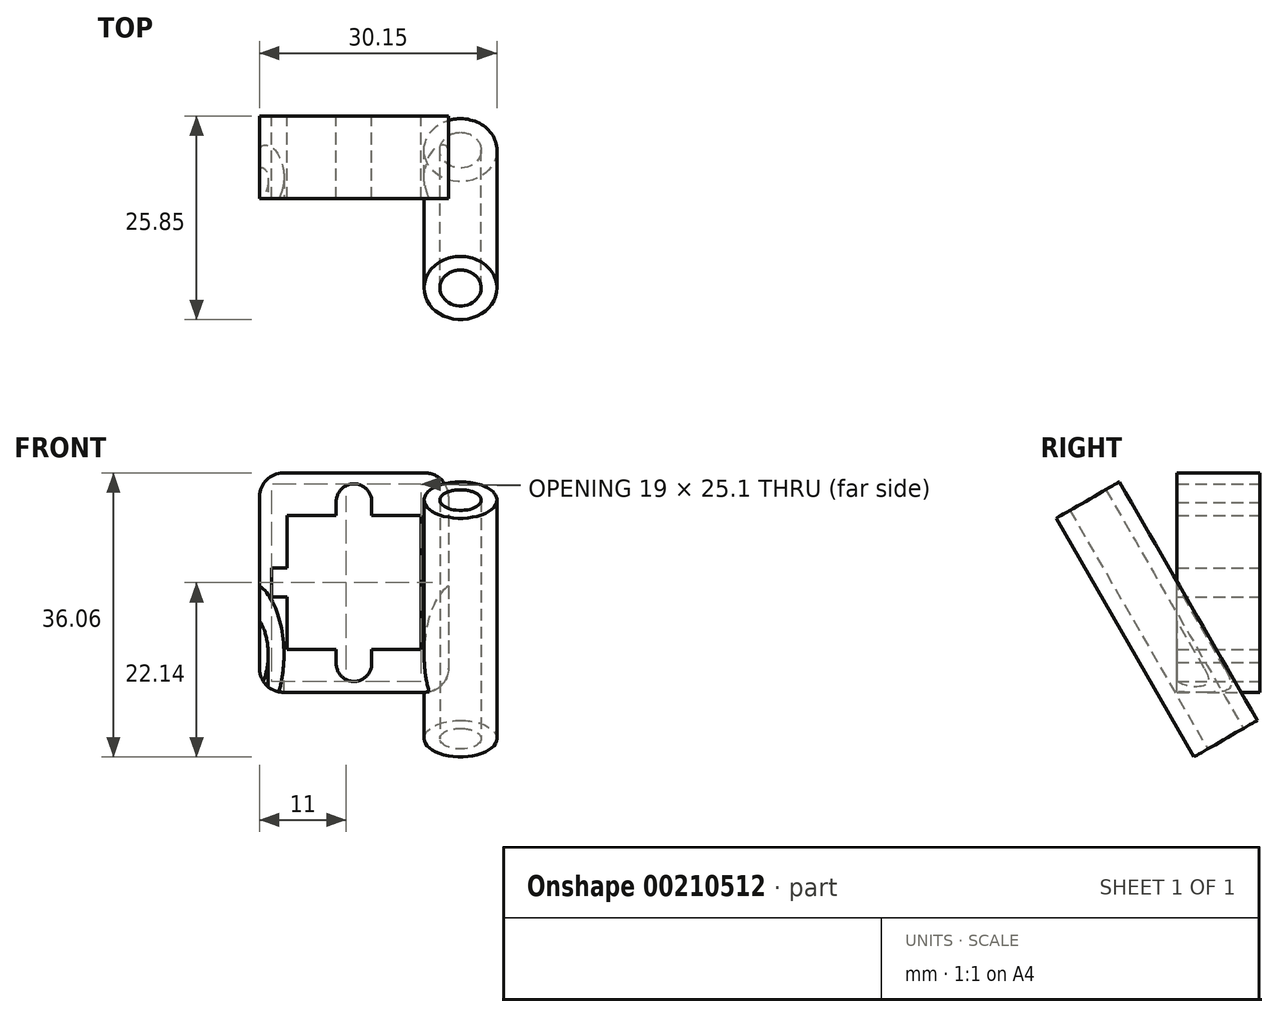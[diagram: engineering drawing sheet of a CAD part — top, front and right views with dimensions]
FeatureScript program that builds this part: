
annotation { "Feature Type Name" : "Feature", "Feature Type Description" : "" }
export const myFeature = defineFeature(function(context is Context, id is Id, definition is map)
    precondition{}
    {
        {
            var Q0;
            Q0=qCreatedBy(makeId("Front.planeOp"),FACE);
            var sketch = newSketch(context, id + "F0", { "sketchPlane" : qUnion([Q0])});
            skLineSegment(sketch, "E0.bottom", {"start": v(8.5, -8.5) * mm, "end": v(2.25, -8.5) * mm});
            skLineSegment(sketch, "E0.top", {"start": v(8.5, 8.5) * mm, "end": v(2.25, 8.5) * mm});
            skLineSegment(sketch, "E0.left", {"start": v(8.5, -8.5) * mm, "end": v(8.5, 8.5) * mm});
            skLineSegment(sketch, "E0.right", {"start": v(-8.5, -8.5) * mm, "end": v(-8.5, -1.85) * mm});
            skPoint(sketch, "E0.middle", {"position": v(0, 0) * mm});
            skLineSegment(sketch, "E1.left", {"start": v(2.25, 10.16) * mm, "end": v(2.25, 8.5) * mm});
            skLineSegment(sketch, "E1.right", {"start": v(-2.25, 10.16) * mm, "end": v(-2.25, 8.5) * mm});
            skLineSegment(sketch, "E2.bottom", {"start": v(-10.5, -1.85) * mm, "end": v(-8.5, -1.85) * mm});
            skLineSegment(sketch, "E2.top", {"start": v(-10.5, 1.85) * mm, "end": v(-8.5, 1.85) * mm});
            skLineSegment(sketch, "E2.left", {"start": v(-10.5, -1.85) * mm, "end": v(-10.5, 1.85) * mm});
            skLineSegment(sketch, "E3.trimOffspring", {"start": v(-2.25, -8.5) * mm, "end": v(-2.25, -10.16) * mm});
            skLineSegment(sketch, "E4.trimOffspring", {"start": v(2.25, -8.5) * mm, "end": v(2.25, -10.16) * mm});
            skLineSegment(sketch, "E5.trimOffspring", {"start": v(-2.25, 8.5) * mm, "end": v(-8.5, 8.5) * mm});
            skLineSegment(sketch, "E6.trimOffspring", {"start": v(-2.25, -8.5) * mm, "end": v(-8.5, -8.5) * mm});
            skLineSegment(sketch, "E7.trimOffspring", {"start": v(-8.5, 1.85) * mm, "end": v(-8.5, 8.5) * mm});
            skArc(sketch, "E8", {"start": v(2.25, 10.16) * mm, "mid": v(0, 12.55) * mm, "end": v(-2.25, 10.16) * mm});
            skPoint(sketch, "E8.first.point", {"position": v(0, 12.55) * mm});
            skPoint(sketch, "E8.second.point", {"position": v(-2.25, 10.16) * mm});
            skPoint(sketch, "E8.third.point", {"position": v(2.25, 10.16) * mm});
            skArc(sketch, "E9.MirrorCS", {"start": v(2.25, -10.16) * mm, "mid": v(0, -12.55) * mm, "end": v(-2.25, -10.16) * mm});
            skLineSegment(sketch, "E10.bottom", {"start": v(9, 13.92) * mm, "end": v(-9, 13.92) * mm});
            skLineSegment(sketch, "E10.top", {"start": v(9, -13.92) * mm, "end": v(-9, -13.92) * mm});
            skLineSegment(sketch, "E10.left", {"start": v(12, 10.92) * mm, "end": v(12, -10.92) * mm});
            skLineSegment(sketch, "E10.right", {"start": v(-12, 10.92) * mm, "end": v(-12, -10.92) * mm});
            skPoint(sketch, "E11.visualSharp", {"position": v(-12, 13.92) * mm});
            skArc(sketch, "E11.filletArc", {"start": v(-9, 13.92) * mm, "mid": v(-11.12, 13.05) * mm, "end": v(-12, 10.92) * mm});
            skPoint(sketch, "E12.visualSharp", {"position": v(12, -13.92) * mm});
            skArc(sketch, "E12.filletArc", {"start": v(9, -13.92) * mm, "mid": v(11.12, -13.05) * mm, "end": v(12, -10.92) * mm});
            skPoint(sketch, "E13.visualSharp", {"position": v(12, 13.92) * mm});
            skArc(sketch, "E13.filletArc", {"start": v(12, 10.92) * mm, "mid": v(11.12, 13.05) * mm, "end": v(9, 13.92) * mm});
            skPoint(sketch, "E14.visualSharp", {"position": v(-12, -13.92) * mm});
            skArc(sketch, "E14.filletArc", {"start": v(-12, -10.92) * mm, "mid": v(-11.12, -13.05) * mm, "end": v(-9, -13.92) * mm});
            skSolve(sketch);
        }
        {
            var Q0;
            Q0=makeQuery(id+"F0.imprint","IMPRINT",FACE,{"disambiguationData":[TD([[makeQuery(id+"F0.imprint","IMPRINT",EDGE,{"derivedFrom":sQuery(id+"F0.wireOp",EDGE,"E0.bottom")}),1.0]])]});
            extrude(context, id + "F1", {"entities" : qUnion([Q0]), "depth" : 10.5 * mm});
        }
        {
            var Q0;
            Q0=qCreatedBy(makeId("Right.planeOp"),FACE);
            var sketch = newSketch(context, id + "F2", { "sketchPlane" : qUnion([Q0])});
            skLineSegment(sketch, "E15", {"start": v(0, 0) * mm, "end": v(-11.77, -6.8) * mm, "construction": true});
            skSolve(sketch);
        }
        {
            var Q0;
            Q0=qCreatedBy(makeId("Front.planeOp"),FACE);
            var Q1;
            Q1=sQuery(id+"F2.wireOp",EDGE,"E15");
            cPlane(context, id + "F3", {"entities" : qUnion([Q0, Q1]), "cplaneType" : CPlaneType.LINE_ANGLE, "offset" : 25 * mm, "angle" : 0 * degree, "width" : 150 * mm, "height" : 150 * mm});
        }
        {
            var Q0;
            Q0=qCreatedBy(id+"F3.planeOp",FACE);
            var sketch = newSketch(context, id + "F4", { "sketchPlane" : qUnion([Q0])});
            skLineSegment(sketch, "E16.bottom", {"start": v(15.94, 11.46) * mm, "end": v(-15.94, 11.46) * mm, "construction": true});
            skLineSegment(sketch, "E16.top", {"start": v(15.94, 15.88) * mm, "end": v(-15.94, 15.88) * mm, "construction": true});
            skLineSegment(sketch, "E16.left", {"start": v(15.94, 11.46) * mm, "end": v(15.94, 15.88) * mm, "construction": true});
            skLineSegment(sketch, "E16.right", {"start": v(-15.94, 11.46) * mm, "end": v(-15.94, 15.88) * mm, "construction": true});
            skPoint(sketch, "E16.middle", {"position": v(0, 13.67) * mm});
            skLineSegment(sketch, "E17", {"start": v(15.94, 11.46) * mm, "end": v(11.1, 15.88) * mm, "construction": true});
            skCircle(sketch, "E18", {"center": v(13.53, 13.67) * mm, "radius": 2.62 * mm});
            skCircle(sketch, "E19.0", {"center": v(13.53, 13.67) * mm, "radius": 4.63 * mm});
            skCircle(sketch, "E20.MirrorC", {"center": v(-13.52, 13.67) * mm, "radius": 4.63 * mm});
            skCircle(sketch, "E21.MirrorC", {"center": v(-13.52, 13.67) * mm, "radius": 2.62 * mm});
            skSolve(sketch);
        }
        {
            var Q0;
            Q0=makeQuery(id+"F4.imprint","IMPRINT",FACE,{"disambiguationData":[TD([[makeQuery(id+"F4.imprint","IMPRINT",EDGE,{"derivedFrom":sQuery(id+"F4.wireOp",EDGE,"E18")}),-1.0]])]});
            var Q1;
            Q1=makeQuery(id+"F4.imprint","IMPRINT",FACE,{"disambiguationData":[TD([[makeQuery(id+"F4.imprint","IMPRINT",EDGE,{"derivedFrom":sQuery(id+"F4.wireOp",EDGE,"E20.MirrorC")}),-1.0]])]});
            extrude(context, id + "F5", {"entities" : qUnion([Q0, Q1]), "operationType" : NewBodyOperationType.ADD, "oppositeDirection" : true, "depth" : 20 * mm, "hasSecondDirection" : true, "secondDirectionOppositeDirection" : false, "secondDirectionDepth" : 15 * mm});
        }
        {
            var Q0;
            Q0=makeQuery(id+"F4.imprint","IMPRINT",FACE,{"disambiguationData":[TD([[makeQuery(id+"F4.imprint","IMPRINT",EDGE,{"derivedFrom":sQuery(id+"F4.wireOp",EDGE,"E21.MirrorC")}),-1.0]])]});
            var Q1;
            Q1=makeQuery(id+"F4.imprint","IMPRINT",FACE,{"disambiguationData":[TD([[makeQuery(id+"F4.imprint","IMPRINT",EDGE,{"derivedFrom":sQuery(id+"F4.wireOp",EDGE,"E18")}),1.0]])]});
            extrude(context, id + "F6", {"entities" : qUnion([Q0, Q1]), "operationType" : NewBodyOperationType.REMOVE, "endBound" : BoundingType.THROUGH_ALL, "depth" : 50 * mm, "hasSecondDirection" : true, "secondDirectionOppositeDirection" : true, "secondDirectionDepth" : 25 * mm});
        }
    });
